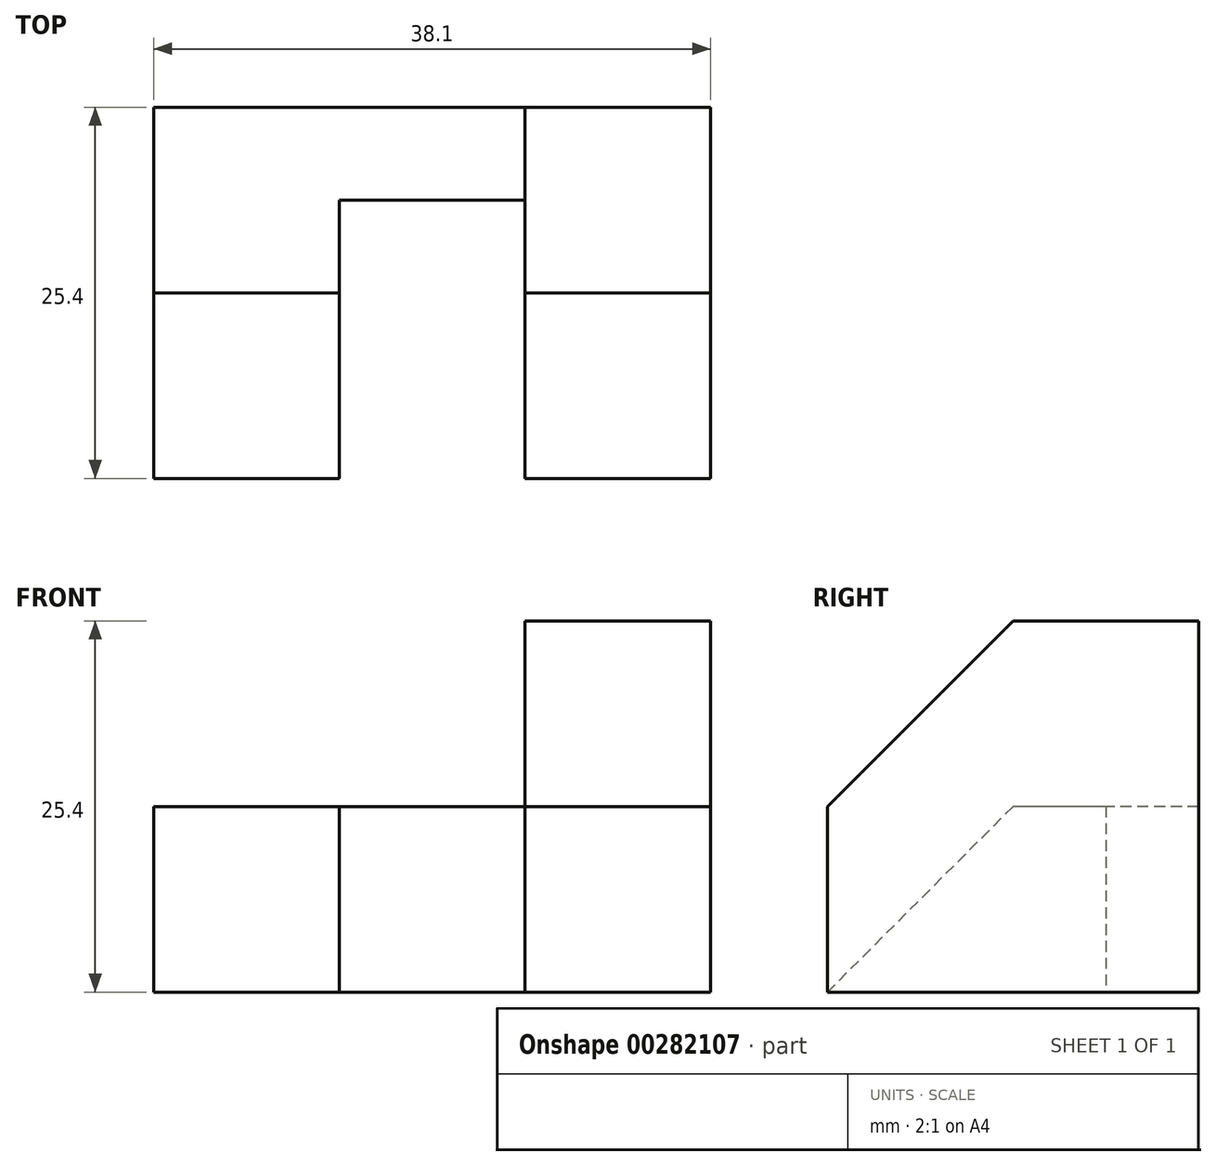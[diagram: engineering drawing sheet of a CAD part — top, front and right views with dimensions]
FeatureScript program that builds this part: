
annotation { "Feature Type Name" : "Feature", "Feature Type Description" : "" }
export const myFeature = defineFeature(function(context is Context, id is Id, definition is map)
    precondition{}
    {
        {
            var Q0;
            Q0=qCreatedBy(makeId("Right.planeOp"),FACE);
            var sketch = newSketch(context, id + "F0", { "sketchPlane" : qUnion([Q0])});
            skLineSegment(sketch, "E0", {"start": v(0, 0) * mm, "end": v(0, 12.7) * mm});
            skLineSegment(sketch, "E1", {"start": v(0, 12.7) * mm, "end": v(12.7, 25.4) * mm});
            skLineSegment(sketch, "E2", {"start": v(12.7, 25.4) * mm, "end": v(25.4, 25.4) * mm});
            skLineSegment(sketch, "E3", {"start": v(25.4, 25.4) * mm, "end": v(25.4, 0) * mm});
            skLineSegment(sketch, "E4", {"start": v(25.4, 0) * mm, "end": v(0, 0) * mm});
            skSolve(sketch);
        }
        {
            var Q0;
            Q0 = qSketchRegion(id + "F0", true);
            extrude(context, id + "F1", {"entities" : qUnion([Q0]), "depth" : 12.7 * mm});
        }
        {
            var Q0;
            Q0=makeQuery(id+"F1.opExtrude","CAP_FACE",FACE,{"disambiguationData":[OSD([sQuery(id+"F0.wireOp",EDGE,"E0"),sQuery(id+"F0.wireOp",EDGE,"E1"),sQuery(id+"F0.wireOp",EDGE,"E2"),sQuery(id+"F0.wireOp",EDGE,"E3"),sQuery(id+"F0.wireOp",EDGE,"E4")])],"isStart":true});
            var sketch = newSketch(context, id + "F2", { "sketchPlane" : qUnion([Q0])});
            skLineSegment(sketch, "E5", {"start": v(-25.4, 12.7) * mm, "end": v(-19.05, 12.7) * mm});
            skLineSegment(sketch, "E6", {"start": v(-19.05, 12.7) * mm, "end": v(-19.05, 0) * mm});
            skLineSegment(sketch, "E7", {"start": v(-19.05, 0) * mm, "end": v(-25.4, 0) * mm});
            skLineSegment(sketch, "E8", {"start": v(-25.4, 0) * mm, "end": v(-25.4, 12.7) * mm});
            skSolve(sketch);
        }
        {
            var Q0;
            Q0 = qSketchRegion(id + "F2", true);
            extrude(context, id + "F3", {"entities" : qUnion([Q0]), "operationType" : NewBodyOperationType.ADD, "depth" : 12.7 * mm});
        }
        {
            var Q0;
            Q0=makeQuery(id+"F3.opExtrude","CAP_FACE",FACE,{"disambiguationData":[OSD([sQuery(id+"F2.wireOp",EDGE,"E5"),sQuery(id+"F2.wireOp",EDGE,"E6"),sQuery(id+"F2.wireOp",EDGE,"E7"),sQuery(id+"F2.wireOp",EDGE,"E8")])],"isStart":false});
            var sketch = newSketch(context, id + "F4", { "sketchPlane" : qUnion([Q0])});
            skLineSegment(sketch, "E9", {"start": v(-25.4, 0) * mm, "end": v(-25.4, 12.7) * mm});
            skLineSegment(sketch, "E10", {"start": v(-25.4, 12.7) * mm, "end": v(-12.7, 12.7) * mm});
            skPoint(sketch, "E10.endSnap0", {"position": v(-22.22, 12.7) * mm});
            skLineSegment(sketch, "E11", {"start": v(-12.7, 12.7) * mm, "end": v(0, 0) * mm});
            skLineSegment(sketch, "E12", {"start": v(0, 0) * mm, "end": v(-25.4, 0) * mm});
            skSolve(sketch);
        }
        {
            var Q0;
            Q0 = qSketchRegion(id + "F4", true);
            extrude(context, id + "F5", {"entities" : qUnion([Q0]), "operationType" : NewBodyOperationType.ADD, "depth" : 12.7 * mm});
        }
    });
